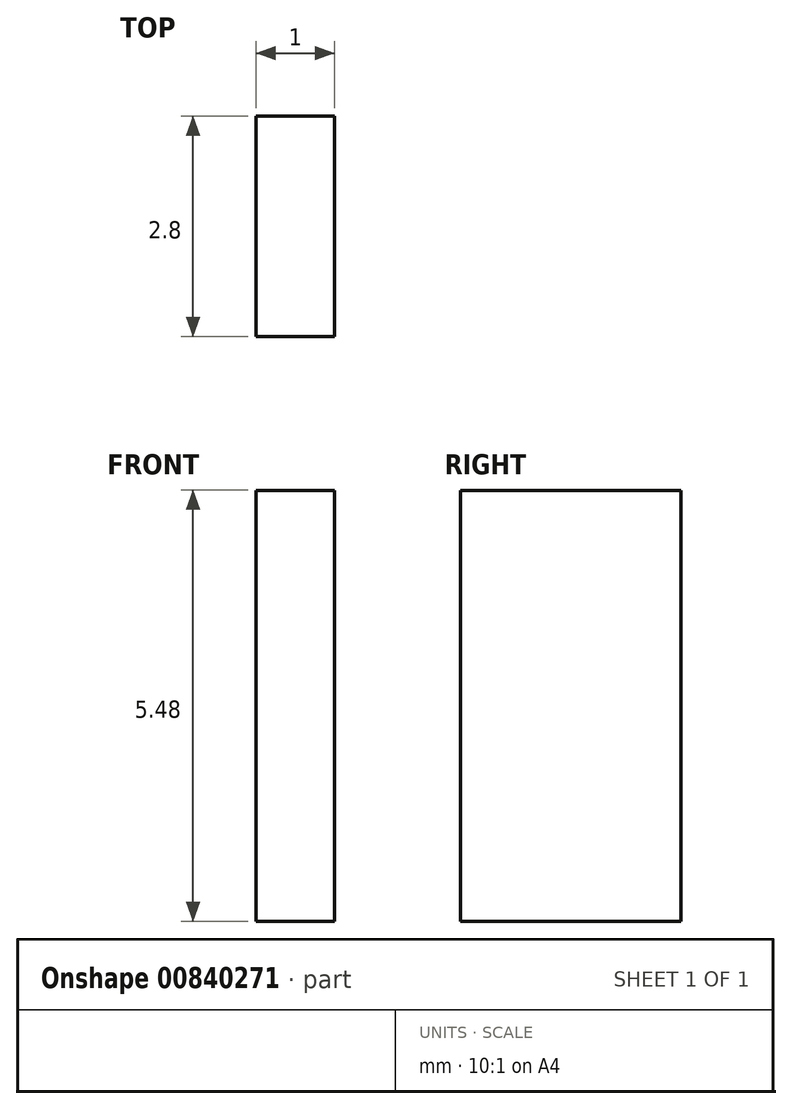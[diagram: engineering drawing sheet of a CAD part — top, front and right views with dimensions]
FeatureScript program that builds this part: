
annotation { "Feature Type Name" : "Feature", "Feature Type Description" : "" }
export const myFeature = defineFeature(function(context is Context, id is Id, definition is map)
    precondition{}
    {
        {
            var Q0;
            Q0=qCreatedBy(makeId("Right.planeOp"),FACE);
            var sketch = newSketch(context, id + "F0", { "sketchPlane" : qUnion([Q0])});
            skLineSegment(sketch, "E0", {"start": v(5.25, -25) * mm, "end": v(6.25, -25) * mm});
            skLineSegment(sketch, "E1.0", {"start": v(4.35, -19.52) * mm, "end": v(4.35, -25) * mm});
            skLineSegment(sketch, "E2.0", {"start": v(7.15, -19.52) * mm, "end": v(7.15, -25) * mm});
            skLineSegment(sketch, "E3", {"start": v(4.35, -25) * mm, "end": v(7.15, -25) * mm});
            skPoint(sketch, "E4.end.orphan", {"position": v(5.75, -25) * mm});
            skLineSegment(sketch, "E5", {"start": v(4.35, -19.52) * mm, "end": v(7.15, -19.52) * mm});
            skSolve(sketch);
        }
        {
            var Q0;
            Q0=makeQuery(id+"F0.imprint","IMPRINT",FACE,{"disambiguationData":[TD([[makeQuery(id+"F0.imprint","IMPRINT",EDGE,{"derivedFrom":sQuery(id+"F0.wireOp",EDGE,"5W6nJ41y-Brwe-AyLZ-LeJi-5wC3d1z5arE5.bottom")}),-1.0]])]});
            var Q1;
            Q1=makeQuery(id+"F0.imprint","IMPRINT",FACE,{"disambiguationData":[TD([[makeQuery(id+"F0.imprint","IMPRINT",EDGE,{"derivedFrom":sQuery(id+"F0.wireOp",EDGE,"qPRy3xUT-NRqM-xTn5-TbLo-p4iQvefC5ACk")}),-1.0]])]});
            var Q2;
            {var subQ3=sQuery(id+"F0.wireOp",EDGE,"63f1d356-c40f-4f39-ade3-4e022c9102be.0");Q2=makeQuery(id+"F0.imprint","IMPRINT",FACE,{"disambiguationData":[TD([[makeQuery(id+"F0.imprint","IMPRINT",EDGE,{"derivedFrom":subQ3}),1.0]])]});}
            var Q3;
            {var subQ3=sQuery(id+"F0.wireOp",EDGE,"fb11080f-c265-4ed2-a8b7-2ce9c9a65e6a.0");Q3=makeQuery(id+"F0.imprint","IMPRINT",FACE,{"disambiguationData":[TD([[makeQuery(id+"F0.imprint","IMPRINT",EDGE,{"derivedFrom":subQ3}),1.0]])]});}
            var Q4;
            {var subQ0=sQuery(id+"F0.wireOp",EDGE,"5dc07093-3f57-4306-a93b-4e72212c7467.0");Q4=makeQuery(id+"F0.imprint","IMPRINT",FACE,{"disambiguationData":[TD([[makeQuery(id+"F0.imprint","IMPRINT",EDGE,{"derivedFrom":subQ0}),1.0]])]});}
            var Q5;
            {var subQ0=sQuery(id+"F0.wireOp",EDGE,"51NmYdBp-mA1z-wu9Q-53MT-rEDAkP0LJ8wn");Q5=makeQuery(id+"F0.imprint","IMPRINT",FACE,{"disambiguationData":[TD([[makeQuery(id+"F0.imprint","IMPRINT",EDGE,{"derivedFrom":subQ0}),-1.0]])]});}
            var Q6;
            {var subQ0=sQuery(id+"F0.wireOp",EDGE,"E1.0");Q6=makeQuery(id+"F0.imprint","IMPRINT",FACE,{"disambiguationData":[TD([[makeQuery(id+"F0.imprint","IMPRINT",EDGE,{"derivedFrom":subQ0}),1.0]])]});}
            extrude(context, id + "F1", {"entities" : qUnion([Q0, Q1, Q2, Q3, Q4, Q5, Q6]), "depth" : 1 * mm, "offsetDistance" : 25 * mm});
        }
    });
